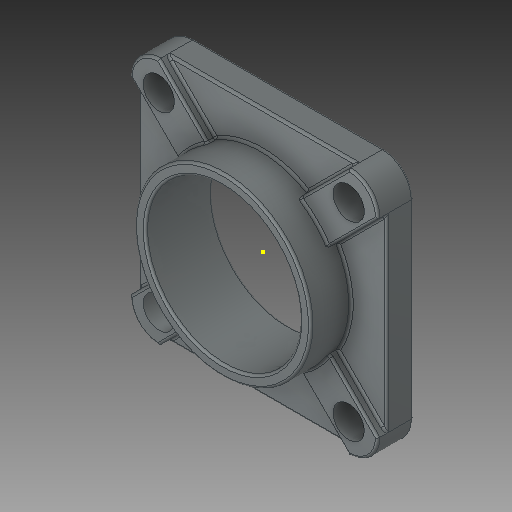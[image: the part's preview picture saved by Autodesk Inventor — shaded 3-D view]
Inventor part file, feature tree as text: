
AUTODESK INVENTOR PART (.ipt)
format: ipt  version: 2019 (Build 230136000, 136)  size: 487,936 bytes
history: native  units: in
note: dims shown in document units (in); Inventor stores cm internally (conversion verified against a paired STEP export)
features: sketch x10, other x3
ambient origin geometry x8: Origin, YZ Plane, XZ Plane, XY Plane, X Axis, Y Axis, Z Axis, Center Point
bodies: Solid1 (feature_tree)
feature tree (13):
  other  "project flange bearing part1_MIR1.ipt"
  other  "Solid1::project flange bearing part1_MIR1.ipt"
  other  "TaggingFeature1"
  sketch  "Sketch1"  dims[d0=0.3937in]
  sketch  "Sketch2"
  sketch  "Sketch3"
  sketch  "Sketch4"
  sketch  "Sketch5"
  sketch  "Sketch6"
  sketch  "Sketch7"
  sketch  "Sketch8"
  sketch  "Sketch9"
  sketch  "Sketch10"
